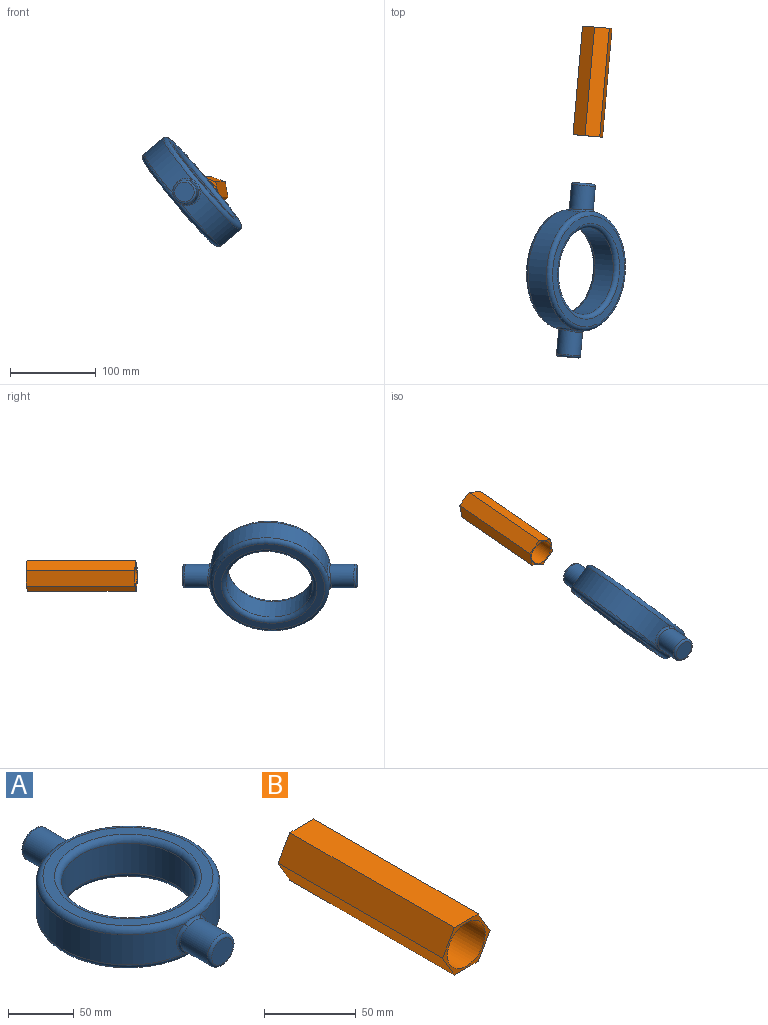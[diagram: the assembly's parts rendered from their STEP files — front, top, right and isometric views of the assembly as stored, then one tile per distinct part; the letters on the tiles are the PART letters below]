
ASSEMBLY  parts=2 mates=1
PART A: 23 faces, bbox 151.2x203.2x38.1 mm
  f0: cylinder r=69.85mm len=138.66mm, axis (0,0,-1), area 5357.9mm2, adj f6,f8,f16,f18
  f1: cylinder r=69.85mm len=138.66mm, axis (0,0,-1), area 5357.9mm2, adj f6,f8,f13,f19
  f2: cylinder r=50.8mm len=101.6mm, axis (0,0,-1), area 8918.1mm2, adj f5,f7
  f3: plane 129.54x129.54mm, normal (0,0,1), area 3369.6mm2, adj f7,f8
  f4: plane 129.54x129.54mm, normal (0,0,-1), area 3369.6mm2, adj f5,f6
  f5: torus R=55.88mm, axis (0,0,1), area 2639.5mm2, adj f2,f4
  f6: torus R=64.77mm, axis (0,0,1), area 3370mm2, adj f0,f1,f4,f14,f17
  f7: torus R=55.88mm, axis (0,0,1), area 2639.5mm2, adj f2,f3
  f8: torus R=64.77mm, axis (0,0,1), area 3370mm2, adj f0,f1,f3,f15,f20
  f9: plane 22.86x22.86mm, normal (0,-1,0), area 410.4mm2, adj f21
  f10: cylinder r=13.97mm len=28.58mm, axis (0,-1,0), area 2431.6mm2, adj f17,f18,f19,f20,f21
  f11: plane 22.86x22.86mm, normal (0,1,0), area 410.4mm2, adj f22
  f12: cylinder r=13.97mm len=28.58mm, axis (0,1,0), area 2431.6mm2, adj f13,f14,f15,f16,f22
  f13: bspline ~29.73x10.04mm, area 107.6mm2, adj f1,f12,f14,f15
  f14: bspline ~20.94x5.12mm, area 54.6mm2, adj f6,f12,f13,f16
  f15: bspline ~20.94x5.12mm, area 54.6mm2, adj f8,f12,f13,f16
  f16: bspline ~29.73x10.04mm, area 107.6mm2, adj f0,f12,f14,f15
  f17: bspline ~20.94x5.12mm, area 54.6mm2, adj f6,f10,f18,f19
  f18: bspline ~29.73x10.04mm, area 107.6mm2, adj f0,f10,f17,f20
  f19: bspline ~29.73x10.04mm, area 107.6mm2, adj f1,f10,f17,f20
  f20: bspline ~20.94x5.12mm, area 54.6mm2, adj f8,f10,f18,f19
  f21: torus R=11.43mm, axis (0,-1,0), area 327.1mm2, adj f9,f10
  f22: torus R=11.43mm, axis (0,-1,0), area 327.1mm2, adj f11,f12
PART B: 10 faces, bbox 36.7x127x31.8 mm
  f0: plane 127x15.88mm, normal (0.87,0,-0.5), area 2328mm2, adj f1,f5,f6,f7
  f1: plane 127x15.88mm, normal (0.87,0,0.5), area 2328mm2, adj f0,f2,f6,f7
  f2: plane 127x18.33mm, normal (0,0,1), area 2328mm2, adj f1,f3,f6,f7
  f3: plane 127x15.88mm, normal (-0.87,0,0.5), area 2328mm2, adj f2,f4,f6,f7
  f4: plane 127x15.88mm, normal (-0.87,0,-0.5), area 2328mm2, adj f3,f5,f6,f7
  f5: plane 127x18.33mm, normal (0,0,-1), area 2328mm2, adj f0,f4,f6,f7
  f6: plane 36.66x31.75mm, normal (0,-1,0), area 202.9mm2, adj f0,f1,f2,f3,f4,f5,f8
  f7: plane 36.66x31.75mm, normal (0,1,0), area 873mm2, adj f0,f1,f2,f3,f4,f5
  f8: cylinder r=14.61mm len=76.2mm, axis (0,-1,0), area 6992.6mm2, adj f6,f9
  f9: plane 29.21x29.21mm, normal (0,-1,0), area 670.1mm2, adj f8
PLACE A rot(axis=(-0.04,-1,-0.02),130.1deg) t=(-251.46,6.67,4.82)mm
PLACE B rot(axis=(0.04,1,-0.02),140deg) t=(-241.25,290.87,-7.42)mm
MATE cylindrical B.f8 <-> A.f10  axis (-0.09,-1,0) through (-252.31,164.35,-7.42)mm
